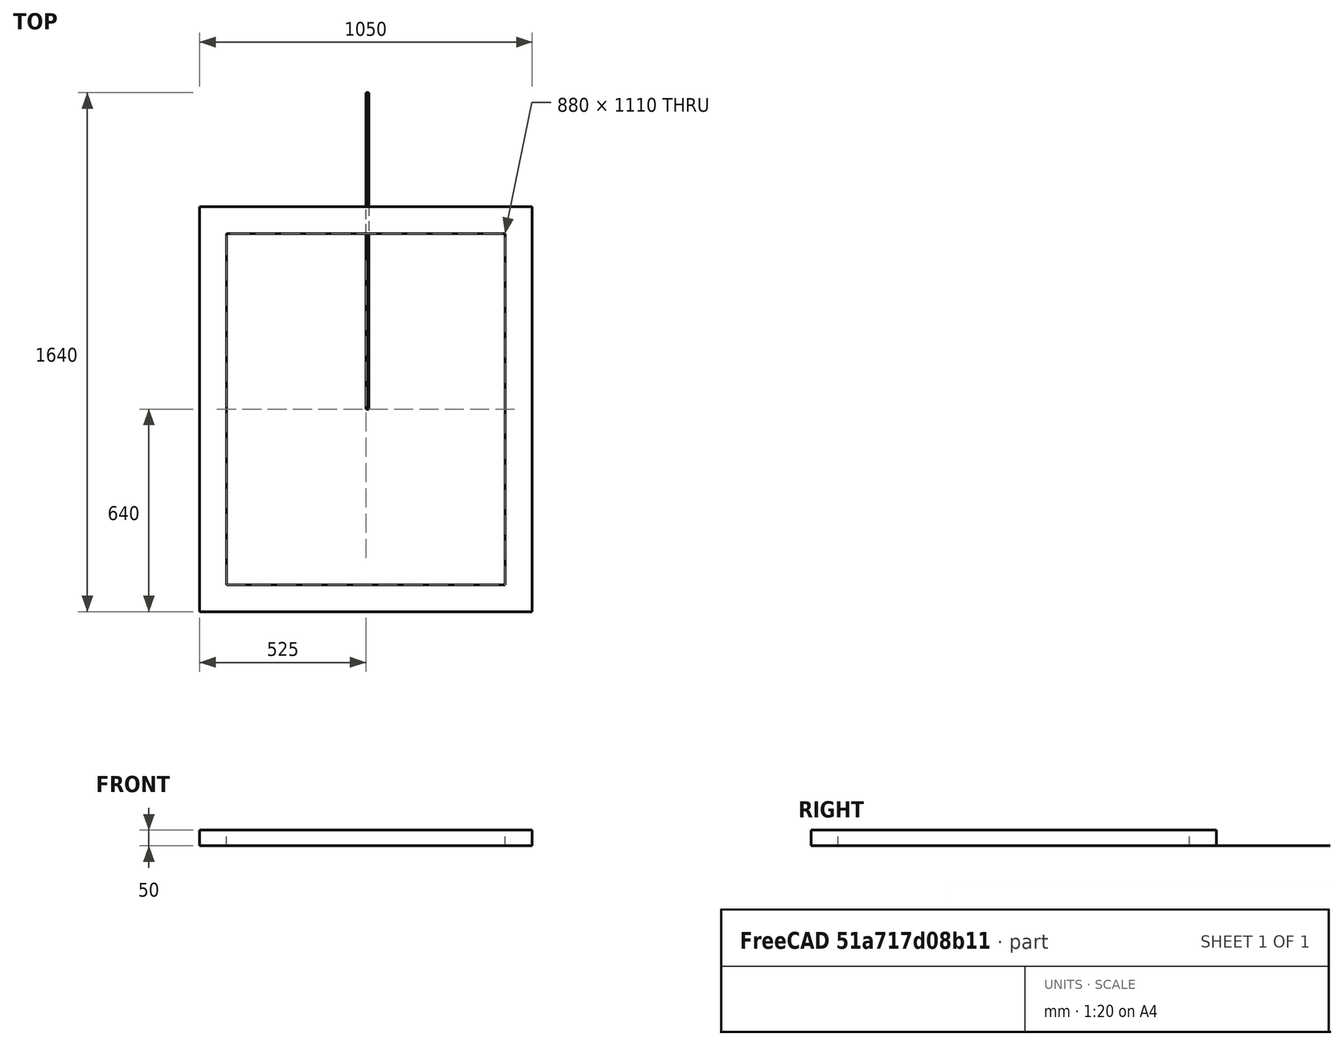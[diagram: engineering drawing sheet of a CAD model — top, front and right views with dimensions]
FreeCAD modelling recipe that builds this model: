
FCSTD DOCUMENT  (FreeCAD 0.19R23578 (Git))
Label: stripes_aufteilung
License: All rights reserved
LicenseURL: http://en.wikipedia.org/wiki/All_rights_reserved
objects: App::FeaturePython×6, Part::FeaturePython×6, TechDraw::DrawViewDimension×4, Sketcher::SketchObject×2, PartDesign::Pad×2, PartDesign::Body×2, TechDraw::DrawSVGTemplate×1, TechDraw::DrawProjGroupItem×1, TechDraw::DrawProjGroup×1, TechDraw::DrawPage×1
note: 11 computed .brp shape members not serialized (recipe doc carries the construction recipe); baked Part::Feature solids carry a one-line shape summary decoded from their .brp

FEATURE [Sketcher::SketchObject] Sketch
  MapMode = 5
  Support = -> [XY_Plane]
  sketch-geometry (8):
    g0: LineSegment StartX=-525 StartY=640 StartZ=0 EndX=525 EndY=640 EndZ=0
    g1: LineSegment StartX=525 StartY=640 StartZ=0 EndX=525 EndY=-640 EndZ=0
    g2: LineSegment StartX=525 StartY=-640 StartZ=0 EndX=-525 EndY=-640 EndZ=0
    g3: LineSegment StartX=-525 StartY=-640 StartZ=0 EndX=-525 EndY=640 EndZ=0
    g4: LineSegment StartX=-440 StartY=555 StartZ=0 EndX=440 EndY=555 EndZ=0
    g5: LineSegment StartX=440 StartY=555 StartZ=0 EndX=440 EndY=-555 EndZ=0
    g6: LineSegment StartX=440 StartY=-555 StartZ=0 EndX=-440 EndY=-555 EndZ=0
    g7: LineSegment StartX=-440 StartY=-555 StartZ=0 EndX=-440 EndY=555 EndZ=0
  constraints (20):
    c: Coincident(g0,g1)
    c: Coincident(g1,g2)
    c: Coincident(g2,g3)
    c: Coincident(g3,g0)
    c: Horizontal(g2)
    c: Vertical(g1)
    c: Coincident(g4,g5)
    c: Coincident(g5,g6)
    c: Coincident(g6,g7)
    c: Coincident(g7,g4)
    c: Horizontal(g6)
    c: Vertical(g5)
    c: Symmetric(g0,g0,g-2)
    c: Symmetric(g4,g4,g-2)
    c: Symmetric(g4,g6,g-1)
    c: Symmetric(g0,g2,g-1)
    c: DistanceY(g1,g1) = 1280
    c: DistanceY(g5,g5) = 1110
    c: DistanceX(g0,g0) = 1050
    c: DistanceX(g4,g4) = 880
FEATURE [PartDesign::Pad] Pad
  Direction = (1,1,1)
  Length = 50
  Length2 = 100
  Profile = -> Sketch
  Type = 0
FEATURE [PartDesign::Body] Body  label="Fensterrahmen"
  Group = -> [Sketch,Pad]
  Origin = -> Origin
  Tip = -> Pad
FEATURE [TechDraw::DrawSVGTemplate] Template
  Height = 297
  Orientation = 1
  Width = 420
FEATURE [TechDraw::DrawProjGroupItem] ProjItem  label="Front"
  CoarseView = false
  Direction = (0,0,1)
  Focus = 100
  HardHidden = false
  IsoCount = 0
  IsoHidden = false
  IsoVisible = false
  LockPosition = true
  Perspective = false
  Rotation = 0
  RotationVector = (1,0,0)
  Scale = 0.15
  ScaleType = 2
  SeamHidden = false
  SeamVisible = true
  SmoothHidden = false
  SmoothVisible = true
  Source = -> [Pad]
  Type = 0
  X = 0
  XDirection = (1,0,0)
  Y = 0
FEATURE [TechDraw::DrawProjGroup] ProjGroup
  Anchor = -> ProjItem
  AutoDistribute = true
  LockPosition = false
  ProjectionType = 0
  Rotation = 0
  Scale = 0.15
  ScaleType = 0
  Source = -> [Pad]
  Views = -> [ProjItem]
  X = 117.933
  Y = 176.022
  spacingX = 15
  spacingY = 15
FEATURE [TechDraw::DrawViewDimension] Dimension
  Arbitrary = false
  ArbitraryTolerances = false
  FormatSpec = %.2f
  FormatSpecOverTolerance = %+.2f
  FormatSpecUnderTolerance = %+.2f
  Inverted = false
  LockPosition = false
  MeasureType = 1
  OverTolerance = 0
  References2D = -> [ProjItem]
  Rotation = 0
  ScaleType = 0
  TheoreticalExact = false
  Type = 1
  UnderTolerance = 0
  X = 0.327641
  Y = -104.874
FEATURE [TechDraw::DrawViewDimension] Dimension001
  Arbitrary = false
  ArbitraryTolerances = false
  FormatSpec = %.2f
  FormatSpecOverTolerance = %+.2f
  FormatSpecUnderTolerance = %+.2f
  Inverted = false
  LockPosition = false
  MeasureType = 1
  OverTolerance = 0
  References2D = -> [ProjItem]
  Rotation = 0
  ScaleType = 0
  TheoreticalExact = false
  Type = 1
  UnderTolerance = 0
  X = -0.327641
  Y = -118.28
FEATURE [TechDraw::DrawViewDimension] Dimension002
  Arbitrary = false
  ArbitraryTolerances = false
  FormatSpec = %.2f
  FormatSpecOverTolerance = %+.2f
  FormatSpecUnderTolerance = %+.2f
  Inverted = false
  LockPosition = false
  MeasureType = 1
  OverTolerance = 0
  References2D = -> [ProjItem]
  Rotation = 0
  ScaleType = 0
  TheoreticalExact = false
  Type = 2
  UnderTolerance = 0
  X = 90.9007
  Y = -2.29348
FEATURE [TechDraw::DrawViewDimension] Dimension003
  Arbitrary = false
  ArbitraryTolerances = false
  FormatSpec = %.2f
  FormatSpecOverTolerance = %+.2f
  FormatSpecUnderTolerance = %+.2f
  Inverted = false
  LockPosition = false
  MeasureType = 1
  OverTolerance = 0
  References2D = -> [ProjItem]
  Rotation = 0
  ScaleType = 0
  TheoreticalExact = false
  Type = 2
  UnderTolerance = 0
  X = 105.944
  Y = -1.96584
FEATURE [TechDraw::DrawPage] Page
  KeepUpdated = true
  NextBalloonIndex = 1
  ProjectionType = 0
  Template = -> Template
  Views = -> [ProjGroup,Dimension,Dimension001,Dimension002,Dimension003]
FEATURE [App::FeaturePython] Constraints  # WARN: FeaturePython — macro-defined, semantics opaque (R4)
  _Version = 1
FEATURE [App::FeaturePython] Elements  # WARN: FeaturePython — macro-defined, semantics opaque (R4)
FEATURE [App::FeaturePython] Constraints001  # WARN: FeaturePython — macro-defined, semantics opaque (R4)
  _Version = 1
FEATURE [App::FeaturePython] Elements001  # WARN: FeaturePython — macro-defined, semantics opaque (R4)
FEATURE [App::FeaturePython] Constraints002  # WARN: FeaturePython — macro-defined, semantics opaque (R4)
  _Version = 1
FEATURE [App::FeaturePython] Elements002  # WARN: FeaturePython — macro-defined, semantics opaque (R4)
FEATURE [Sketcher::SketchObject] Sketch001
  MapMode = 5
  Support = -> [XY_Plane001]
  sketch-geometry (4):
    g0: LineSegment StartX=0 StartY=1000 StartZ=0 EndX=10 EndY=1000 EndZ=0
    g1: LineSegment StartX=10 StartY=1000 StartZ=0 EndX=10 EndY=0 EndZ=0
    g2: LineSegment StartX=10 StartY=0 StartZ=0 EndX=0 EndY=0 EndZ=0
    g3: LineSegment StartX=0 StartY=0 StartZ=0 EndX=0 EndY=1000 EndZ=0
  constraints (11):
    c: Coincident(g0,g1)
    c: Coincident(g1,g2)
    c: Coincident(g2,g3)
    c: Coincident(g3,g0)
    c: Horizontal(g0)
    c: Horizontal(g2)
    c: Vertical(g1)
    c: Vertical(g3)
    c: DistanceY(g1,g1) = 1000
    c: DistanceX(g0,g0) = 10
    c: Coincident(g2,g-1)
FEATURE [PartDesign::Pad] Pad001
  Direction = (1,1,1)
  Length = 0.5
  Length2 = 100
  Profile = -> Sketch001
  Type = 0
FEATURE [PartDesign::Body] Body001
  Group = -> [Sketch001,Pad001]
  Origin = -> Origin001
  Tip = -> Pad001
FEATURE [Part::FeaturePython] Parts002  # WARN: FeaturePython — macro-defined, semantics opaque (R4)
  Group = -> [Body001]
  GroupMode = 0
FEATURE [Part::FeaturePython] Assembly002  label="Stripe"  # WARN: FeaturePython — macro-defined, semantics opaque (R4)
  AutoRelax = true
  BuildShape = 0
  Freeze = false
  Group = -> [Constraints002,Elements002,Parts002]
  Verbose = false
  _SolverType = 1
  _Version = 1
FEATURE [Part::FeaturePython] Parts001  # WARN: FeaturePython — macro-defined, semantics opaque (R4)
  Group = -> [Assembly002]
  GroupMode = 0
FEATURE [Part::FeaturePython] Assembly001  label="Stipes"  # WARN: FeaturePython — macro-defined, semantics opaque (R4)
  AutoRelax = true
  BuildShape = 0
  Freeze = false
  Group = -> [Constraints001,Elements001,Parts001]
  Placement = pos=(-287.904,-509.673,0) rot=(0,0,1;0rad)
  Verbose = false
  _SolverType = 1
  _Version = 1
FEATURE [Part::FeaturePython] Parts  # WARN: FeaturePython — macro-defined, semantics opaque (R4)
  Group = -> [Body,Assembly001]
  GroupMode = 0
FEATURE [Part::FeaturePython] Assembly  # WARN: FeaturePython — macro-defined, semantics opaque (R4)
  AutoRelax = true
  BuildShape = 0
  Freeze = false
  Group = -> [Constraints,Elements,Parts]
  Verbose = false
  _SolverType = 1
  _Version = 1
